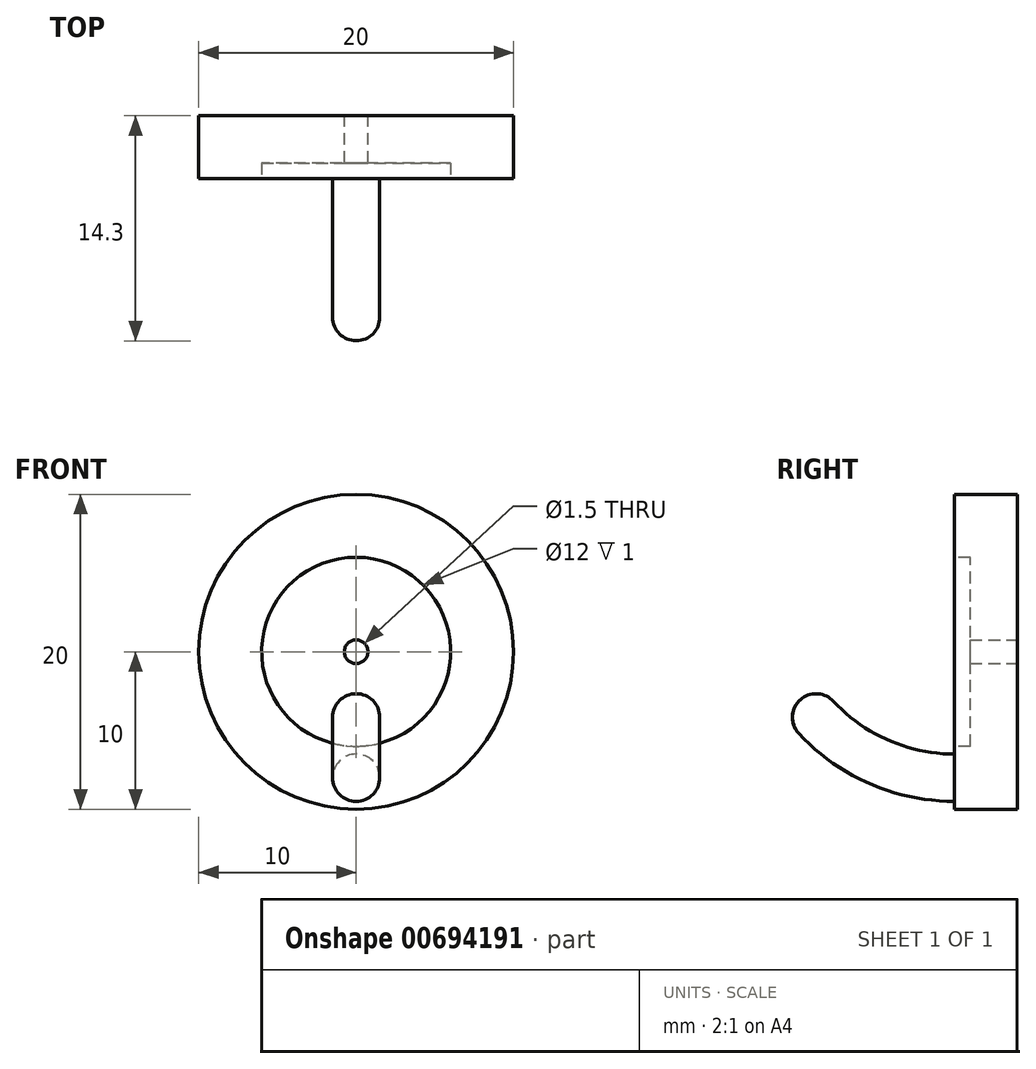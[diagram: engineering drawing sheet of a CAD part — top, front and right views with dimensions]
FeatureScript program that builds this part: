
annotation { "Feature Type Name" : "Feature", "Feature Type Description" : "" }
export const myFeature = defineFeature(function(context is Context, id is Id, definition is map)
    precondition{}
    {
        {
            var Q0;
            Q0=qCreatedBy(makeId("Front.planeOp"),FACE);
            var sketch = newSketch(context, id + "F0", { "sketchPlane" : qUnion([Q0])});
            skLineSegment(sketch, "E0.bottom", {"start": v(10, 10) * mm, "end": v(-10, 10) * mm});
            skLineSegment(sketch, "E0.top", {"start": v(10, -10) * mm, "end": v(-10, -10) * mm});
            skLineSegment(sketch, "E0.left", {"start": v(10, 10) * mm, "end": v(10, -10) * mm});
            skLineSegment(sketch, "E0.right", {"start": v(-10, 10) * mm, "end": v(-10, -10) * mm});
            skPoint(sketch, "E0.middle", {"position": v(0, 0) * mm});
            skCircle(sketch, "E1", {"center": v(0, 0) * mm, "radius": 0.75 * mm});
            skSolve(sketch);
        }
        {
            var Q0;
            Q0=makeQuery(id+"F0.imprint","IMPRINT",FACE,{"disambiguationData":[TD([[makeQuery(id+"F0.imprint","IMPRINT",EDGE,{"derivedFrom":sQuery(id+"F0.wireOp",EDGE,"E0.bottom")}),1.0]])]});
            extrude(context, id + "F1", {"entities" : qUnion([Q0]), "depth" : 4 * mm, "offsetDistance" : 25 * mm});
        }
        {
            var Q0;
            Q0=makeQuery(id+"F1.opExtrude","CAP_FACE",FACE,{"disambiguationData":[OSD([sQuery(id+"F0.wireOp",EDGE,"E0.bottom"),sQuery(id+"F0.wireOp",EDGE,"E0.top"),sQuery(id+"F0.wireOp",EDGE,"E0.left"),sQuery(id+"F0.wireOp",EDGE,"E0.right"),sQuery(id+"F0.wireOp",EDGE,"E1")])],"isStart":false});
            var sketch = newSketch(context, id + "F2", { "sketchPlane" : qUnion([Q0])});
            skCircle(sketch, "E2", {"center": v(0, 0) * mm, "radius": 6 * mm});
            skSolve(sketch);
        }
        {
            var Q0;
            Q0=makeQuery(id+"F2.imprint","IMPRINT",FACE,{"disambiguationData":[TD([[makeQuery(id+"F2.imprint","IMPRINT",EDGE,{"derivedFrom":sQuery(id+"F2.wireOp",EDGE,"E2")}),1.0]])]});
            extrude(context, id + "F3", {"entities" : qUnion([Q0]), "operationType" : NewBodyOperationType.REMOVE, "oppositeDirection" : true, "depth" : 1 * mm, "offsetDistance" : 25 * mm});
        }
        {
            var Q0;
            Q0=makeQuery(id+"F1.opExtrude","CAP_FACE",FACE,{"disambiguationData":[OSD([sQuery(id+"F0.wireOp",EDGE,"E0.bottom"),sQuery(id+"F0.wireOp",EDGE,"E0.top"),sQuery(id+"F0.wireOp",EDGE,"E0.left"),sQuery(id+"F0.wireOp",EDGE,"E0.right"),sQuery(id+"F0.wireOp",EDGE,"E1")])],"isStart":false});
            var sketch = newSketch(context, id + "F4", { "sketchPlane" : qUnion([Q0])});
            skCircle(sketch, "E3", {"center": v(0, -8) * mm, "radius": 1.5 * mm});
            skSolve(sketch);
        }
        {
            var Q0;
            Q0=qCreatedBy(makeId("Right.planeOp"),FACE);
            var sketch = newSketch(context, id + "F5", { "sketchPlane" : qUnion([Q0])});
            skArc(sketch, "E4", {"start": v(-13.75, -3) * mm, "mid": v(-9.48, -6.68) * mm, "end": v(-4, -8) * mm});
            skSolve(sketch);
        }
        {
            var Q0;
            Q0=makeQuery(id+"F4.imprint","IMPRINT",FACE,{"disambiguationData":[TD([[makeQuery(id+"F4.imprint","IMPRINT",EDGE,{"derivedFrom":sQuery(id+"F4.wireOp",EDGE,"E3")}),1.0]])]});
            var Q1;
            Q1=sQuery(id+"F5.wireOp",EDGE,"E4");
            sweep(context, id + "F6", {"operationType" : NewBodyOperationType.ADD, "profiles" : qUnion([Q0]), "path" : qUnion([Q1])});
        }
        {
            var Q0;
            Q0=makeQuery(id+"F6.opSweep","CAP_EDGE",EDGE,{"disambiguationData":[OSD([sQuery(id+"F4.wireOp",EDGE,"E3"),sQuery(id+"F5.wireOp",VERTEX,"E4.start")])],"isStart":false});
            fillet(context, id + "F7", {"entities" : qUnion([Q0]), "radius" : 1.5 * mm, "tangentPropagation" : true, "allowEdgeOverflow" : false});
        }
        {
            var Q0;
            Q0=makeQuery(id+"F1.opExtrude","SWEPT_EDGE",EDGE,{"disambiguationData":[OSD([sQuery(id+"F0.wireOp",EDGE,"E0.bottom"),sQuery(id+"F0.wireOp",EDGE,"E0.right")])]});
            var Q1;
            Q1=makeQuery(id+"F1.opExtrude","SWEPT_EDGE",EDGE,{"disambiguationData":[OSD([sQuery(id+"F0.wireOp",EDGE,"E0.bottom"),sQuery(id+"F0.wireOp",EDGE,"E0.left")])]});
            var Q2;
            Q2=makeQuery(id+"F1.opExtrude","SWEPT_EDGE",EDGE,{"disambiguationData":[OSD([sQuery(id+"F0.wireOp",EDGE,"E0.top"),sQuery(id+"F0.wireOp",EDGE,"E0.left")])]});
            var Q3;
            Q3=makeQuery(id+"F1.opExtrude","SWEPT_EDGE",EDGE,{"disambiguationData":[OSD([sQuery(id+"F0.wireOp",EDGE,"E0.top"),sQuery(id+"F0.wireOp",EDGE,"E0.right")])]});
            fillet(context, id + "F8", {"entities" : qUnion([Q0, Q1, Q2, Q3]), "radius" : 10 * mm, "tangentPropagation" : true, "allowEdgeOverflow" : false});
        }
    });
